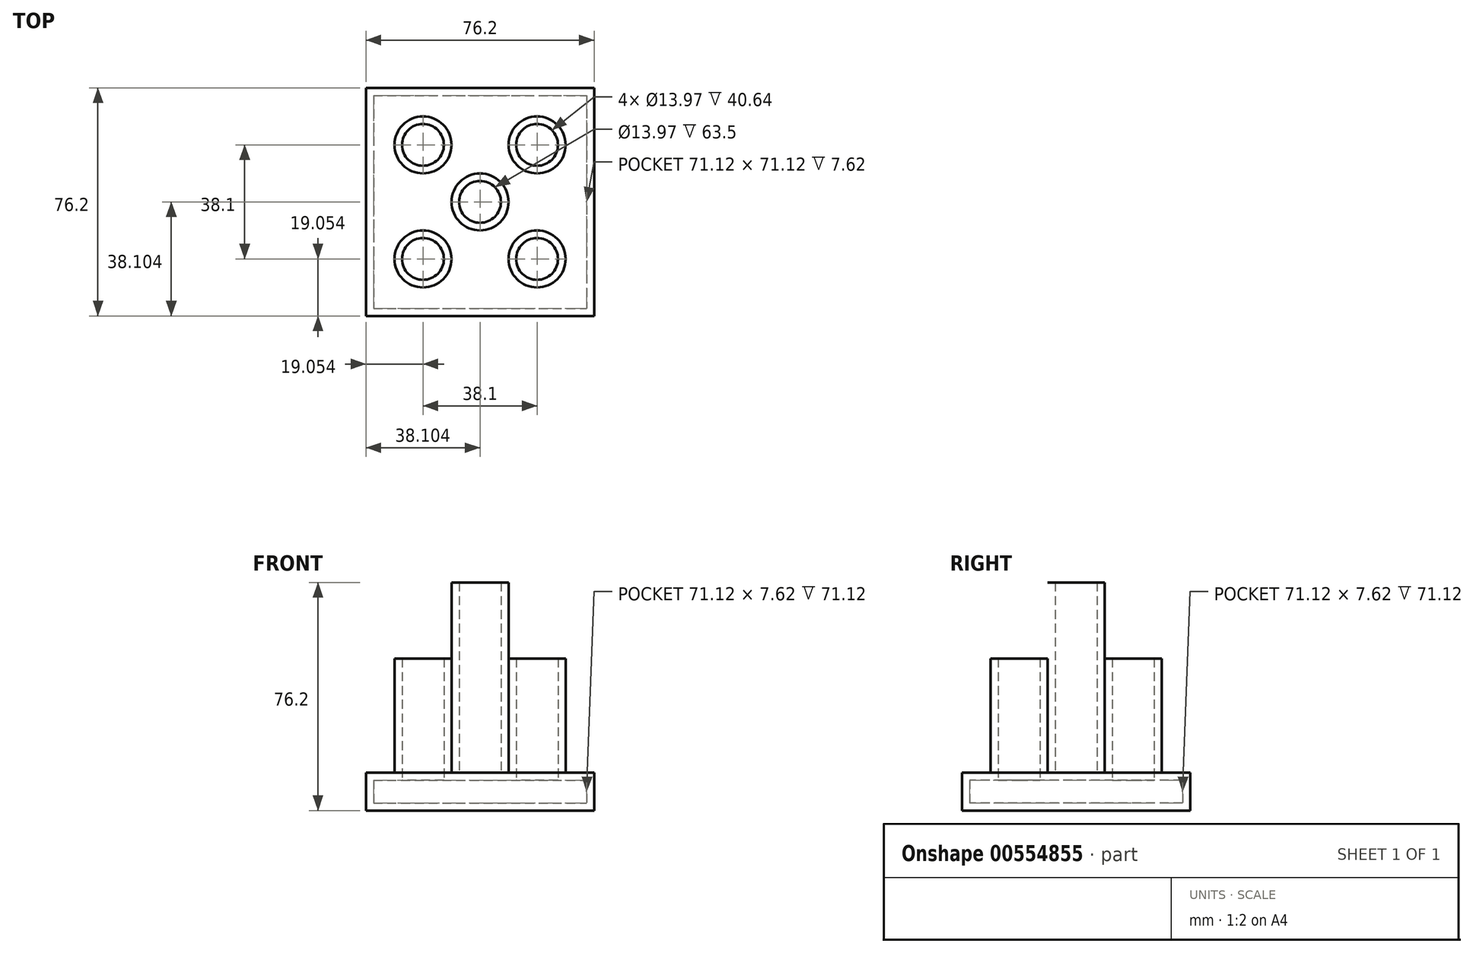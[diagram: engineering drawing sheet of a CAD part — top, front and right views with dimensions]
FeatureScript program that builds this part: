
annotation { "Feature Type Name" : "Feature", "Feature Type Description" : "" }
export const myFeature = defineFeature(function(context is Context, id is Id, definition is map)
    precondition{}
    {
        {
            var Q0;
            Q0=qCreatedBy(makeId("Top.planeOp"),FACE);
            var sketch = newSketch(context, id + "F0", { "sketchPlane" : qUnion([Q0])});
            skLineSegment(sketch, "E0.bottom", {"start": v(-57.04, 32.58) * mm, "end": v(19.16, 32.58) * mm});
            skLineSegment(sketch, "E0.top", {"start": v(-57.04, -43.62) * mm, "end": v(19.16, -43.62) * mm});
            skLineSegment(sketch, "E0.left", {"start": v(-57.04, 32.58) * mm, "end": v(-57.04, -43.62) * mm});
            skLineSegment(sketch, "E0.right", {"start": v(19.16, 32.58) * mm, "end": v(19.16, -43.62) * mm});
            skLineSegment(sketch, "E1", {"start": v(-57.04, -5.52) * mm, "end": v(-57.04, 32.58) * mm});
            skLineSegment(sketch, "E2", {"start": v(-57.04, -5.52) * mm, "end": v(-57.04, -43.62) * mm});
            skLineSegment(sketch, "E3", {"start": v(19.16, -43.62) * mm, "end": v(19.16, -5.52) * mm});
            skLineSegment(sketch, "E4", {"start": v(19.16, -5.52) * mm, "end": v(19.16, 32.58) * mm});
            skLineSegment(sketch, "E5", {"start": v(-57.04, 32.58) * mm, "end": v(-18.94, 32.58) * mm});
            skPoint(sketch, "E6.centerSnap0", {"position": v(-37.99, 32.58) * mm});
            skPoint(sketch, "E6.centerSnap1", {"position": v(-57.04, 13.53) * mm});
            skLineSegment(sketch, "E7", {"start": v(-18.94, 32.58) * mm, "end": v(19.16, 32.58) * mm});
            skPoint(sketch, "E8.centerSnap0", {"position": v(19.16, 13.53) * mm});
            skPoint(sketch, "E8.centerSnap1", {"position": v(0.11, 32.58) * mm});
            skLineSegment(sketch, "E9", {"start": v(-57.04, -43.62) * mm, "end": v(-18.94, -43.62) * mm});
            skPoint(sketch, "E10.centerSnap0", {"position": v(-37.99, -43.62) * mm});
            skPoint(sketch, "E10.centerSnap1", {"position": v(-57.04, -24.57) * mm});
            skPoint(sketch, "E11.centerSnap0", {"position": v(19.16, -24.57) * mm});
            skSolve(sketch);
        }
        {
            var Q0;
            Q0=makeQuery(id+"F0.imprint","IMPRINT",FACE,{"disambiguationData":[TD([[makeQuery(id+"F0.imprint","IMPRINT",EDGE,{"derivedFrom":sQuery(id+"F0.wireOp",EDGE,"E0.top")}),1.0]])]});
            extrude(context, id + "F1", {"entities" : qUnion([Q0]), "depth" : 12.7 * mm, "offsetDistance" : 25.4 * mm});
        }
        {
            var Q0;
            Q0=makeQuery(id+"F1.opExtrude","CAP_FACE",FACE,{"disambiguationData":[OSD([sQuery(id+"F0.wireOp",EDGE,"E0.top"),sQuery(id+"F0.wireOp",EDGE,"E1"),sQuery(id+"F0.wireOp",EDGE,"E2"),sQuery(id+"F0.wireOp",EDGE,"E3"),sQuery(id+"F0.wireOp",EDGE,"E4"),sQuery(id+"F0.wireOp",EDGE,"E5"),sQuery(id+"F0.wireOp",EDGE,"E7"),sQuery(id+"F0.wireOp",EDGE,"E9")])],"isStart":false});
            var sketch = newSketch(context, id + "F2", { "sketchPlane" : qUnion([Q0])});
            skLineSegment(sketch, "E12", {"start": v(-57.04, 32.58) * mm, "end": v(19.16, 32.58) * mm});
            skLineSegment(sketch, "E13", {"start": v(19.16, 32.58) * mm, "end": v(19.16, -43.62) * mm});
            skLineSegment(sketch, "E14", {"start": v(19.16, -43.62) * mm, "end": v(-57.04, -43.62) * mm});
            skLineSegment(sketch, "E15", {"start": v(-57.04, -43.62) * mm, "end": v(-57.04, 32.58) * mm});
            skLineSegment(sketch, "E16", {"start": v(-57.04, -5.52) * mm, "end": v(-57.04, -43.62) * mm});
            skLineSegment(sketch, "E17", {"start": v(-18.94, -43.62) * mm, "end": v(19.16, -43.62) * mm});
            skLineSegment(sketch, "E18", {"start": v(19.16, -5.52) * mm, "end": v(19.16, 32.58) * mm});
            skLineSegment(sketch, "E19", {"start": v(-18.94, 32.58) * mm, "end": v(-57.04, 32.58) * mm});
            skLineSegment(sketch, "E20", {"start": v(-57.04, -5.52) * mm, "end": v(-57.04, 32.58) * mm});
            skCircle(sketch, "E21", {"center": v(-37.99, 13.53) * mm, "radius": 9.53 * mm});
            skPoint(sketch, "E21.centerSnap0", {"position": v(-57.04, 13.53) * mm});
            skPoint(sketch, "E21.centerSnap1", {"position": v(-37.99, 32.58) * mm});
            skLineSegment(sketch, "E22", {"start": v(-18.94, 32.58) * mm, "end": v(19.16, 32.58) * mm});
            skCircle(sketch, "E23", {"center": v(0.11, 13.53) * mm, "radius": 9.53 * mm});
            skPoint(sketch, "E23.centerSnap0", {"position": v(0.11, 32.58) * mm});
            skPoint(sketch, "E23.centerSnap1", {"position": v(19.16, 13.53) * mm});
            skLineSegment(sketch, "E24", {"start": v(-18.94, -43.62) * mm, "end": v(-57.04, -43.62) * mm});
            skCircle(sketch, "E25", {"center": v(-37.99, -24.57) * mm, "radius": 9.53 * mm});
            skPoint(sketch, "E25.centerSnap0", {"position": v(-37.99, -43.62) * mm});
            skPoint(sketch, "E25.centerSnap1", {"position": v(-57.04, -24.57) * mm});
            skLineSegment(sketch, "E26", {"start": v(19.16, -5.52) * mm, "end": v(19.16, -43.62) * mm});
            skCircle(sketch, "E27", {"center": v(0.11, -24.57) * mm, "radius": 9.53 * mm});
            skPoint(sketch, "E27.centerSnap0", {"position": v(19.16, -24.57) * mm});
            skPoint(sketch, "E27.centerSnap1", {"position": v(0.11, -43.62) * mm});
            skSolve(sketch);
        }
        {
            var Q0;
            Q0=makeQuery(id+"F2.imprint","IMPRINT",FACE,{"disambiguationData":[TD([[makeQuery(id+"F2.imprint","IMPRINT",EDGE,{"derivedFrom":sQuery(id+"F2.wireOp",EDGE,"E21")}),1.0]])]});
            var Q1;
            Q1=makeQuery(id+"F2.imprint","IMPRINT",FACE,{"disambiguationData":[TD([[makeQuery(id+"F2.imprint","IMPRINT",EDGE,{"derivedFrom":sQuery(id+"F2.wireOp",EDGE,"E23")}),1.0]])]});
            var Q2;
            Q2=makeQuery(id+"F2.imprint","IMPRINT",FACE,{"disambiguationData":[TD([[makeQuery(id+"F2.imprint","IMPRINT",EDGE,{"derivedFrom":sQuery(id+"F2.wireOp",EDGE,"E25")}),1.0]])]});
            var Q3;
            Q3=makeQuery(id+"F2.imprint","IMPRINT",FACE,{"disambiguationData":[TD([[makeQuery(id+"F2.imprint","IMPRINT",EDGE,{"derivedFrom":sQuery(id+"F2.wireOp",EDGE,"E27")}),1.0]])]});
            extrude(context, id + "F3", {"entities" : qUnion([Q0, Q1, Q2, Q3]), "operationType" : NewBodyOperationType.ADD, "depth" : 38.1 * mm, "offsetDistance" : 25.4 * mm});
        }
        {
            var Q0;
            Q0=makeQuery(id+"F3.opExtrude","CAP_FACE",FACE,{"disambiguationData":[OSD([sQuery(id+"F2.wireOp",EDGE,"E23")])],"isStart":false});
            var Q1;
            Q1=makeQuery(id+"F3.opExtrude","CAP_FACE",FACE,{"disambiguationData":[OSD([sQuery(id+"F2.wireOp",EDGE,"E27")])],"isStart":false});
            var Q2;
            Q2=makeQuery(id+"F3.opExtrude","CAP_FACE",FACE,{"disambiguationData":[OSD([sQuery(id+"F2.wireOp",EDGE,"E25")])],"isStart":false});
            var Q3;
            Q3=makeQuery(id+"F3.opExtrude","CAP_FACE",FACE,{"disambiguationData":[OSD([sQuery(id+"F2.wireOp",EDGE,"E21")])],"isStart":false});
            shell(context, id + "F4", {"entities" : qUnion([Q0, Q1, Q2, Q3]), "thickness" : 2.54 * mm});
        }
        {
            var Q0;
            Q0=makeQuery(id+"F1.opExtrude","CAP_FACE",FACE,{"disambiguationData":[OSD([sQuery(id+"F0.wireOp",EDGE,"E0.top"),sQuery(id+"F0.wireOp",EDGE,"E1"),sQuery(id+"F0.wireOp",EDGE,"E2"),sQuery(id+"F0.wireOp",EDGE,"E3"),sQuery(id+"F0.wireOp",EDGE,"E4"),sQuery(id+"F0.wireOp",EDGE,"E5"),sQuery(id+"F0.wireOp",EDGE,"E7"),sQuery(id+"F0.wireOp",EDGE,"E9")])],"isStart":false});
            var sketch = newSketch(context, id + "F5", { "sketchPlane" : qUnion([Q0])});
            skCircle(sketch, "E28", {"center": v(-18.94, -5.52) * mm, "radius": 9.53 * mm});
            skPoint(sketch, "E28.centerSnap0", {"position": v(-57.04, -5.52) * mm});
            skPoint(sketch, "E28.centerSnap1", {"position": v(-18.94, 32.58) * mm});
            skSolve(sketch);
        }
        {
            var Q0;
            Q0=makeQuery(id+"F5.imprint","IMPRINT",FACE,{"disambiguationData":[TD([[makeQuery(id+"F5.imprint","IMPRINT",EDGE,{"derivedFrom":sQuery(id+"F5.wireOp",EDGE,"E28")}),1.0]])]});
            extrude(context, id + "F6", {"entities" : qUnion([Q0]), "operationType" : NewBodyOperationType.ADD, "depth" : 63.5 * mm, "offsetDistance" : 25.4 * mm});
        }
        {
            var Q0;
            Q0=makeQuery(id+"F6.opExtrude","CAP_FACE",FACE,{"disambiguationData":[OSD([sQuery(id+"F5.wireOp",EDGE,"E28")])],"isStart":false});
            shell(context, id + "F7", {"entities" : qUnion([Q0]), "thickness" : 2.54 * mm});
        }
    });
